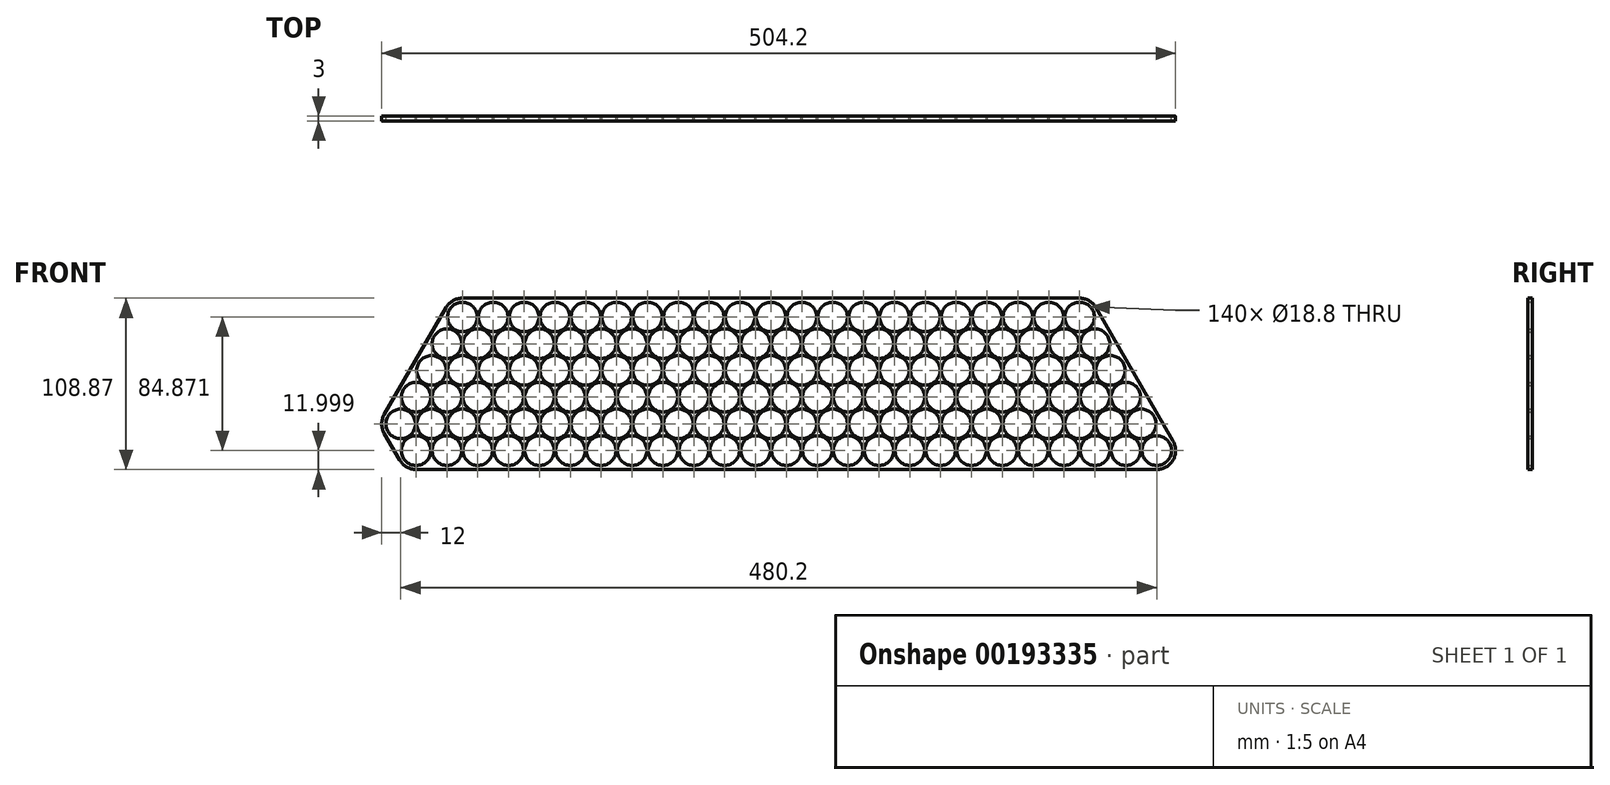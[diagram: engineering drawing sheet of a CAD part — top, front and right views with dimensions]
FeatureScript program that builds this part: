
annotation { "Feature Type Name" : "Feature", "Feature Type Description" : "" }
export const myFeature = defineFeature(function(context is Context, id is Id, definition is map)
    precondition{}
    {
        {
            var Q0;
            Q0=qCreatedBy(makeId("Front.planeOp"),FACE);
            var sketch = newSketch(context, id + "F0", { "sketchPlane" : qUnion([Q0])});
            skLineSegment(sketch, "E0", {"start": v(0, 0) * mm, "end": v(79.44, 0) * mm, "construction": true});
            skLineSegment(sketch, "E1", {"start": v(0, 0) * mm, "end": v(43.4, -75.16) * mm, "construction": true});
            skCircle(sketch, "E2", {"center": v(0, 0) * mm, "radius": 9.4 * mm});
            skCircle(sketch, "E3.1.0.0", {"center": v(19.6, 0) * mm, "radius": 9.4 * mm});
            skCircle(sketch, "E3.2.0.0", {"center": v(39.2, 0) * mm, "radius": 9.4 * mm});
            skCircle(sketch, "E3.3.0.0", {"center": v(58.8, 0) * mm, "radius": 9.4 * mm});
            skCircle(sketch, "E3.4.0.0", {"center": v(78.4, 0) * mm, "radius": 9.4 * mm});
            skCircle(sketch, "E3.5.0.0", {"center": v(98, 0) * mm, "radius": 9.4 * mm});
            skCircle(sketch, "E3.6.0.0", {"center": v(117.6, 0) * mm, "radius": 9.4 * mm});
            skCircle(sketch, "E3.7.0.0", {"center": v(137.2, 0) * mm, "radius": 9.4 * mm});
            skCircle(sketch, "E3.8.0.0", {"center": v(156.8, 0) * mm, "radius": 9.4 * mm});
            skCircle(sketch, "E3.9.0.0", {"center": v(176.4, 0) * mm, "radius": 9.4 * mm});
            skCircle(sketch, "E3.10.0.0", {"center": v(196, 0) * mm, "radius": 9.4 * mm});
            skCircle(sketch, "E3.11.0.0", {"center": v(215.6, 0) * mm, "radius": 9.4 * mm});
            skCircle(sketch, "E3.12.0.0", {"center": v(235.2, 0) * mm, "radius": 9.4 * mm});
            skCircle(sketch, "E3.13.0.0", {"center": v(254.8, 0) * mm, "radius": 9.4 * mm});
            skCircle(sketch, "E3.14.0.0", {"center": v(274.4, 0) * mm, "radius": 9.4 * mm});
            skCircle(sketch, "E3.15.0.0", {"center": v(294, 0) * mm, "radius": 9.4 * mm});
            skCircle(sketch, "E3.16.0.0", {"center": v(313.6, 0) * mm, "radius": 9.4 * mm});
            skCircle(sketch, "E3.17.0.0", {"center": v(333.2, 0) * mm, "radius": 9.4 * mm});
            skCircle(sketch, "E3.18.0.0", {"center": v(352.8, 0) * mm, "radius": 9.4 * mm});
            skCircle(sketch, "E3.19.0.0", {"center": v(372.4, 0) * mm, "radius": 9.4 * mm});
            skLineSegment(sketch, "E3.direction1", {"start": v(0, 0) * mm, "end": v(19.6, 0) * mm, "construction": true});
            skCircle(sketch, "E4.1.0.0", {"center": v(9.8, -16.97) * mm, "radius": 9.4 * mm});
            skCircle(sketch, "E4.2.0.0", {"center": v(19.6, -33.95) * mm, "radius": 9.4 * mm});
            skCircle(sketch, "E4.3.0.0", {"center": v(29.4, -50.92) * mm, "radius": 9.4 * mm});
            skCircle(sketch, "E4.4.0.0", {"center": v(39.2, -67.9) * mm, "radius": 9.4 * mm});
            skCircle(sketch, "E4.5.0.0", {"center": v(49, -84.87) * mm, "radius": 9.4 * mm});
            skLineSegment(sketch, "E4.direction1", {"start": v(0, 0) * mm, "end": v(9.8, -16.97) * mm, "construction": true});
            skCircle(sketch, "E5.1.0.0", {"center": v(29.4, -16.97) * mm, "radius": 9.4 * mm});
            skCircle(sketch, "E5.1.0.1", {"center": v(39.2, -33.95) * mm, "radius": 9.4 * mm});
            skCircle(sketch, "E5.1.0.2", {"center": v(49, -50.92) * mm, "radius": 9.4 * mm});
            skCircle(sketch, "E5.1.0.3", {"center": v(58.8, -67.9) * mm, "radius": 9.4 * mm});
            skCircle(sketch, "E5.1.0.4", {"center": v(68.6, -84.87) * mm, "radius": 9.4 * mm});
            skCircle(sketch, "E5.2.0.0", {"center": v(49, -16.97) * mm, "radius": 9.4 * mm});
            skCircle(sketch, "E5.2.0.1", {"center": v(58.8, -33.95) * mm, "radius": 9.4 * mm});
            skCircle(sketch, "E5.2.0.2", {"center": v(68.6, -50.92) * mm, "radius": 9.4 * mm});
            skCircle(sketch, "E5.2.0.3", {"center": v(78.4, -67.9) * mm, "radius": 9.4 * mm});
            skCircle(sketch, "E5.2.0.4", {"center": v(88.2, -84.87) * mm, "radius": 9.4 * mm});
            skCircle(sketch, "E5.3.0.0", {"center": v(68.6, -16.97) * mm, "radius": 9.4 * mm});
            skCircle(sketch, "E5.3.0.1", {"center": v(78.4, -33.95) * mm, "radius": 9.4 * mm});
            skCircle(sketch, "E5.3.0.2", {"center": v(88.2, -50.92) * mm, "radius": 9.4 * mm});
            skCircle(sketch, "E5.3.0.3", {"center": v(98, -67.9) * mm, "radius": 9.4 * mm});
            skCircle(sketch, "E5.3.0.4", {"center": v(107.8, -84.87) * mm, "radius": 9.4 * mm});
            skCircle(sketch, "E5.4.0.0", {"center": v(88.2, -16.97) * mm, "radius": 9.4 * mm});
            skCircle(sketch, "E5.4.0.1", {"center": v(98, -33.95) * mm, "radius": 9.4 * mm});
            skCircle(sketch, "E5.4.0.2", {"center": v(107.8, -50.92) * mm, "radius": 9.4 * mm});
            skCircle(sketch, "E5.4.0.3", {"center": v(117.6, -67.9) * mm, "radius": 9.4 * mm});
            skCircle(sketch, "E5.4.0.4", {"center": v(127.4, -84.87) * mm, "radius": 9.4 * mm});
            skCircle(sketch, "E5.5.0.0", {"center": v(107.8, -16.97) * mm, "radius": 9.4 * mm});
            skCircle(sketch, "E5.5.0.1", {"center": v(117.6, -33.95) * mm, "radius": 9.4 * mm});
            skCircle(sketch, "E5.5.0.2", {"center": v(127.4, -50.92) * mm, "radius": 9.4 * mm});
            skCircle(sketch, "E5.5.0.3", {"center": v(137.2, -67.9) * mm, "radius": 9.4 * mm});
            skCircle(sketch, "E5.5.0.4", {"center": v(147, -84.87) * mm, "radius": 9.4 * mm});
            skCircle(sketch, "E5.6.0.0", {"center": v(127.4, -16.97) * mm, "radius": 9.4 * mm});
            skCircle(sketch, "E5.6.0.1", {"center": v(137.2, -33.95) * mm, "radius": 9.4 * mm});
            skCircle(sketch, "E5.6.0.2", {"center": v(147, -50.92) * mm, "radius": 9.4 * mm});
            skCircle(sketch, "E5.6.0.3", {"center": v(156.8, -67.9) * mm, "radius": 9.4 * mm});
            skCircle(sketch, "E5.6.0.4", {"center": v(166.6, -84.87) * mm, "radius": 9.4 * mm});
            skCircle(sketch, "E5.7.0.0", {"center": v(147, -16.97) * mm, "radius": 9.4 * mm});
            skCircle(sketch, "E5.7.0.1", {"center": v(156.8, -33.95) * mm, "radius": 9.4 * mm});
            skCircle(sketch, "E5.7.0.2", {"center": v(166.6, -50.92) * mm, "radius": 9.4 * mm});
            skCircle(sketch, "E5.7.0.3", {"center": v(176.4, -67.9) * mm, "radius": 9.4 * mm});
            skCircle(sketch, "E5.7.0.4", {"center": v(186.2, -84.87) * mm, "radius": 9.4 * mm});
            skCircle(sketch, "E5.8.0.0", {"center": v(166.6, -16.97) * mm, "radius": 9.4 * mm});
            skCircle(sketch, "E5.8.0.1", {"center": v(176.4, -33.95) * mm, "radius": 9.4 * mm});
            skCircle(sketch, "E5.8.0.2", {"center": v(186.2, -50.92) * mm, "radius": 9.4 * mm});
            skCircle(sketch, "E5.8.0.3", {"center": v(196, -67.9) * mm, "radius": 9.4 * mm});
            skCircle(sketch, "E5.8.0.4", {"center": v(205.8, -84.87) * mm, "radius": 9.4 * mm});
            skCircle(sketch, "E5.9.0.0", {"center": v(186.2, -16.97) * mm, "radius": 9.4 * mm});
            skCircle(sketch, "E5.9.0.1", {"center": v(196, -33.95) * mm, "radius": 9.4 * mm});
            skCircle(sketch, "E5.9.0.2", {"center": v(205.8, -50.92) * mm, "radius": 9.4 * mm});
            skCircle(sketch, "E5.9.0.3", {"center": v(215.6, -67.9) * mm, "radius": 9.4 * mm});
            skCircle(sketch, "E5.9.0.4", {"center": v(225.4, -84.87) * mm, "radius": 9.4 * mm});
            skCircle(sketch, "E5.10.0.0", {"center": v(205.8, -16.97) * mm, "radius": 9.4 * mm});
            skCircle(sketch, "E5.10.0.1", {"center": v(215.6, -33.95) * mm, "radius": 9.4 * mm});
            skCircle(sketch, "E5.10.0.2", {"center": v(225.4, -50.92) * mm, "radius": 9.4 * mm});
            skCircle(sketch, "E5.10.0.3", {"center": v(235.2, -67.9) * mm, "radius": 9.4 * mm});
            skCircle(sketch, "E5.10.0.4", {"center": v(245, -84.87) * mm, "radius": 9.4 * mm});
            skCircle(sketch, "E5.11.0.0", {"center": v(225.4, -16.97) * mm, "radius": 9.4 * mm});
            skCircle(sketch, "E5.11.0.1", {"center": v(235.2, -33.95) * mm, "radius": 9.4 * mm});
            skCircle(sketch, "E5.11.0.2", {"center": v(245, -50.92) * mm, "radius": 9.4 * mm});
            skCircle(sketch, "E5.11.0.3", {"center": v(254.8, -67.9) * mm, "radius": 9.4 * mm});
            skCircle(sketch, "E5.11.0.4", {"center": v(264.6, -84.87) * mm, "radius": 9.4 * mm});
            skCircle(sketch, "E5.12.0.0", {"center": v(245, -16.97) * mm, "radius": 9.4 * mm});
            skCircle(sketch, "E5.12.0.1", {"center": v(254.8, -33.95) * mm, "radius": 9.4 * mm});
            skCircle(sketch, "E5.12.0.2", {"center": v(264.6, -50.92) * mm, "radius": 9.4 * mm});
            skCircle(sketch, "E5.12.0.3", {"center": v(274.4, -67.9) * mm, "radius": 9.4 * mm});
            skCircle(sketch, "E5.12.0.4", {"center": v(284.2, -84.87) * mm, "radius": 9.4 * mm});
            skCircle(sketch, "E5.13.0.0", {"center": v(264.6, -16.97) * mm, "radius": 9.4 * mm});
            skCircle(sketch, "E5.13.0.1", {"center": v(274.4, -33.95) * mm, "radius": 9.4 * mm});
            skCircle(sketch, "E5.13.0.2", {"center": v(284.2, -50.92) * mm, "radius": 9.4 * mm});
            skCircle(sketch, "E5.13.0.3", {"center": v(294, -67.9) * mm, "radius": 9.4 * mm});
            skCircle(sketch, "E5.13.0.4", {"center": v(303.8, -84.87) * mm, "radius": 9.4 * mm});
            skCircle(sketch, "E5.14.0.0", {"center": v(284.2, -16.97) * mm, "radius": 9.4 * mm});
            skCircle(sketch, "E5.14.0.1", {"center": v(294, -33.95) * mm, "radius": 9.4 * mm});
            skCircle(sketch, "E5.14.0.2", {"center": v(303.8, -50.92) * mm, "radius": 9.4 * mm});
            skCircle(sketch, "E5.14.0.3", {"center": v(313.6, -67.9) * mm, "radius": 9.4 * mm});
            skCircle(sketch, "E5.14.0.4", {"center": v(323.4, -84.87) * mm, "radius": 9.4 * mm});
            skCircle(sketch, "E5.15.0.0", {"center": v(303.8, -16.97) * mm, "radius": 9.4 * mm});
            skCircle(sketch, "E5.15.0.1", {"center": v(313.6, -33.95) * mm, "radius": 9.4 * mm});
            skCircle(sketch, "E5.15.0.2", {"center": v(323.4, -50.92) * mm, "radius": 9.4 * mm});
            skCircle(sketch, "E5.15.0.3", {"center": v(333.2, -67.9) * mm, "radius": 9.4 * mm});
            skCircle(sketch, "E5.15.0.4", {"center": v(343, -84.87) * mm, "radius": 9.4 * mm});
            skCircle(sketch, "E5.16.0.0", {"center": v(323.4, -16.97) * mm, "radius": 9.4 * mm});
            skCircle(sketch, "E5.16.0.1", {"center": v(333.2, -33.95) * mm, "radius": 9.4 * mm});
            skCircle(sketch, "E5.16.0.2", {"center": v(343, -50.92) * mm, "radius": 9.4 * mm});
            skCircle(sketch, "E5.16.0.3", {"center": v(352.8, -67.9) * mm, "radius": 9.4 * mm});
            skCircle(sketch, "E5.16.0.4", {"center": v(362.6, -84.87) * mm, "radius": 9.4 * mm});
            skCircle(sketch, "E5.17.0.0", {"center": v(343, -16.97) * mm, "radius": 9.4 * mm});
            skCircle(sketch, "E5.17.0.1", {"center": v(352.8, -33.95) * mm, "radius": 9.4 * mm});
            skCircle(sketch, "E5.17.0.2", {"center": v(362.6, -50.92) * mm, "radius": 9.4 * mm});
            skCircle(sketch, "E5.17.0.3", {"center": v(372.4, -67.9) * mm, "radius": 9.4 * mm});
            skCircle(sketch, "E5.17.0.4", {"center": v(382.2, -84.87) * mm, "radius": 9.4 * mm});
            skCircle(sketch, "E5.18.0.0", {"center": v(362.6, -16.97) * mm, "radius": 9.4 * mm});
            skCircle(sketch, "E5.18.0.1", {"center": v(372.4, -33.95) * mm, "radius": 9.4 * mm});
            skCircle(sketch, "E5.18.0.2", {"center": v(382.2, -50.92) * mm, "radius": 9.4 * mm});
            skCircle(sketch, "E5.18.0.3", {"center": v(392, -67.9) * mm, "radius": 9.4 * mm});
            skCircle(sketch, "E5.18.0.4", {"center": v(401.8, -84.87) * mm, "radius": 9.4 * mm});
            skCircle(sketch, "E5.19.0.0", {"center": v(382.2, -16.97) * mm, "radius": 9.4 * mm});
            skCircle(sketch, "E5.19.0.1", {"center": v(392, -33.95) * mm, "radius": 9.4 * mm});
            skCircle(sketch, "E5.19.0.2", {"center": v(401.8, -50.92) * mm, "radius": 9.4 * mm});
            skCircle(sketch, "E5.19.0.3", {"center": v(411.6, -67.9) * mm, "radius": 9.4 * mm});
            skCircle(sketch, "E5.19.0.4", {"center": v(421.4, -84.87) * mm, "radius": 9.4 * mm});
            skLineSegment(sketch, "E5.direction1", {"start": v(9.8, -16.97) * mm, "end": v(29.4, -16.97) * mm, "construction": true});
            skLineSegment(sketch, "E6", {"start": v(0, 0) * mm, "end": v(372.4, 0) * mm, "construction": true});
            skLineSegment(sketch, "E7", {"start": v(372.4, 0) * mm, "end": v(421.4, -84.87) * mm, "construction": true});
            skLineSegment(sketch, "E8", {"start": v(49, -84.87) * mm, "end": v(0, 0) * mm, "construction": true});
            skLineSegment(sketch, "E9.0", {"start": v(-20.78, 12) * mm, "end": v(372.4, 12) * mm});
            skLineSegment(sketch, "E9.1", {"start": v(42.07, -96.87) * mm, "end": v(-20.78, 12) * mm, "construction": true});
            skLineSegment(sketch, "E10", {"start": v(49, -84.87) * mm, "end": v(421.4, -84.87) * mm, "construction": true});
            skLineSegment(sketch, "E11.0", {"start": v(49, -96.87) * mm, "end": v(421.4, -96.87) * mm});
            skLineSegment(sketch, "E12", {"start": v(49, -96.87) * mm, "end": v(42.07, -96.87) * mm});
            skLineSegment(sketch, "E13", {"start": v(42.07, -96.87) * mm, "end": v(-49, -96.87) * mm});
            skPoint(sketch, "E13.endSnap0", {"position": v(45.54, -96.87) * mm});
            skLineSegment(sketch, "E14", {"start": v(-20.78, 12) * mm, "end": v(-20.84, 11.94) * mm});
            skCircle(sketch, "E15.1.0.0", {"center": v(29.4, -84.87) * mm, "radius": 9.4 * mm});
            skCircle(sketch, "E15.2.0.0", {"center": v(9.8, -84.87) * mm, "radius": 9.4 * mm});
            skCircle(sketch, "E15.3.0.0", {"center": v(-9.8, -84.87) * mm, "radius": 9.4 * mm});
            skCircle(sketch, "E15.4.0.0", {"center": v(-29.4, -84.87) * mm, "radius": 9.4 * mm});
            skCircle(sketch, "E15.5.0.0", {"center": v(-49, -84.87) * mm, "radius": 9.4 * mm});
            skLineSegment(sketch, "E15.direction1", {"start": v(49, -84.87) * mm, "end": v(29.4, -84.87) * mm, "construction": true});
            skCircle(sketch, "E16.1.0.0", {"center": v(19.6, -67.9) * mm, "radius": 9.4 * mm});
            skCircle(sketch, "E16.2.0.0", {"center": v(0, -67.9) * mm, "radius": 9.4 * mm});
            skCircle(sketch, "E16.3.0.0", {"center": v(-19.6, -67.9) * mm, "radius": 9.4 * mm});
            skCircle(sketch, "E16.4.0.0", {"center": v(-39.2, -67.9) * mm, "radius": 9.4 * mm});
            skCircle(sketch, "E16.5.0.0", {"center": v(-58.8, -67.9) * mm, "radius": 9.4 * mm});
            skLineSegment(sketch, "E16.direction1", {"start": v(39.2, -67.9) * mm, "end": v(19.6, -67.9) * mm, "construction": true});
            skCircle(sketch, "E17.1.0.0", {"center": v(9.8, -50.92) * mm, "radius": 9.4 * mm});
            skCircle(sketch, "E17.2.0.0", {"center": v(-9.8, -50.92) * mm, "radius": 9.4 * mm});
            skCircle(sketch, "E17.3.0.0", {"center": v(-29.4, -50.92) * mm, "radius": 9.4 * mm});
            skCircle(sketch, "E17.4.0.0", {"center": v(-49, -50.92) * mm, "radius": 9.4 * mm});
            skLineSegment(sketch, "E17.direction1", {"start": v(29.4, -50.92) * mm, "end": v(9.8, -50.92) * mm, "construction": true});
            skCircle(sketch, "E18.1.0.0", {"center": v(0, -33.95) * mm, "radius": 9.4 * mm});
            skCircle(sketch, "E18.2.0.0", {"center": v(-19.6, -33.95) * mm, "radius": 9.4 * mm});
            skCircle(sketch, "E18.3.0.0", {"center": v(-39.2, -33.95) * mm, "radius": 9.4 * mm});
            skLineSegment(sketch, "E18.direction1", {"start": v(19.6, -33.95) * mm, "end": v(0, -33.95) * mm, "construction": true});
            skCircle(sketch, "E19.1.0.0", {"center": v(-9.8, -16.97) * mm, "radius": 9.4 * mm});
            skCircle(sketch, "E19.2.0.0", {"center": v(-29.4, -16.97) * mm, "radius": 9.4 * mm});
            skLineSegment(sketch, "E19.direction1", {"start": v(9.8, -16.97) * mm, "end": v(-9.8, -16.97) * mm, "construction": true});
            skCircle(sketch, "E20.1.0.0", {"center": v(-19.6, 0) * mm, "radius": 9.4 * mm});
            skLineSegment(sketch, "E20.direction1", {"start": v(0, 0) * mm, "end": v(-19.6, 0) * mm, "construction": true});
            skArc(sketch, "E21.0", {"start": v(-19.6, 12) * mm, "mid": v(-25.6, 10.4) * mm, "end": v(-30, 6) * mm});
            skLineSegment(sketch, "E22", {"start": v(-30, 6) * mm, "end": v(-69.2, -61.9) * mm});
            skPoint(sketch, "E23.orphan", {"position": v(-115.18, -96.87) * mm});
            skArc(sketch, "E24.trimOffspring", {"start": v(-69.2, -61.9) * mm, "mid": v(-70.8, -67.9) * mm, "end": v(-69.2, -73.9) * mm});
            skLineSegment(sketch, "E25", {"start": v(-59.4, -90.87) * mm, "end": v(-69.2, -73.9) * mm});
            skArc(sketch, "E26.trimOffspring", {"start": v(-59.4, -90.87) * mm, "mid": v(-55, -95.26) * mm, "end": v(-49, -96.87) * mm});
            skArc(sketch, "E27", {"start": v(421.4, -96.87) * mm, "mid": v(431.8, -90.87) * mm, "end": v(431.8, -78.87) * mm});
            skArc(sketch, "E28", {"start": v(382.8, 6) * mm, "mid": v(378.4, 10.4) * mm, "end": v(372.4, 12) * mm});
            skLineSegment(sketch, "E29", {"start": v(431.8, -78.87) * mm, "end": v(382.8, 6) * mm});
            skSolve(sketch);
        }
        {
            var Q0;
            Q0=makeQuery(id+"F0.imprint","IMPRINT",FACE,{"disambiguationData":[TD([[makeQuery(id+"F0.imprint","IMPRINT",EDGE,{"derivedFrom":sQuery(id+"F0.wireOp",EDGE,"E2")}),-1.0]])]});
            extrude(context, id + "F1", {"entities" : qUnion([Q0]), "depth" : 3 * mm});
        }
        {
            var Q0;
            Q0=makeQuery(id+"F0.imprint","IMPRINT",FACE,{"disambiguationData":[TD([[makeQuery(id+"F0.imprint","IMPRINT",EDGE,{"derivedFrom":sQuery(id+"F0.wireOp",EDGE,"E2")}),-1.0]])]});
            var Q1;
            Q1=makeQuery(id+"F0.imprint","IMPRINT",FACE,{"disambiguationData":[TD([[makeQuery(id+"F0.imprint","IMPRINT",EDGE,{"derivedFrom":sQuery(id+"F0.wireOp",EDGE,"E3.19.0.0")}),1.0]])]});
            var Q2;
            Q2=makeQuery(id+"F0.imprint","IMPRINT",FACE,{"disambiguationData":[TD([[makeQuery(id+"F0.imprint","IMPRINT",EDGE,{"derivedFrom":sQuery(id+"F0.wireOp",EDGE,"E3.18.0.0")}),1.0]])]});
            var Q3;
            Q3=makeQuery(id+"F0.imprint","IMPRINT",FACE,{"disambiguationData":[TD([[makeQuery(id+"F0.imprint","IMPRINT",EDGE,{"derivedFrom":sQuery(id+"F0.wireOp",EDGE,"E3.17.0.0")}),1.0]])]});
            var Q4;
            Q4=makeQuery(id+"F0.imprint","IMPRINT",FACE,{"disambiguationData":[TD([[makeQuery(id+"F0.imprint","IMPRINT",EDGE,{"derivedFrom":sQuery(id+"F0.wireOp",EDGE,"E3.16.0.0")}),1.0]])]});
            var Q5;
            Q5=makeQuery(id+"F0.imprint","IMPRINT",FACE,{"disambiguationData":[TD([[makeQuery(id+"F0.imprint","IMPRINT",EDGE,{"derivedFrom":sQuery(id+"F0.wireOp",EDGE,"E3.15.0.0")}),1.0]])]});
            var Q6;
            Q6=makeQuery(id+"F0.imprint","IMPRINT",FACE,{"disambiguationData":[TD([[makeQuery(id+"F0.imprint","IMPRINT",EDGE,{"derivedFrom":sQuery(id+"F0.wireOp",EDGE,"E3.14.0.0")}),1.0]])]});
            var Q7;
            Q7=makeQuery(id+"F0.imprint","IMPRINT",FACE,{"disambiguationData":[TD([[makeQuery(id+"F0.imprint","IMPRINT",EDGE,{"derivedFrom":sQuery(id+"F0.wireOp",EDGE,"E3.13.0.0")}),1.0]])]});
            var Q8;
            Q8=makeQuery(id+"F0.imprint","IMPRINT",FACE,{"disambiguationData":[TD([[makeQuery(id+"F0.imprint","IMPRINT",EDGE,{"derivedFrom":sQuery(id+"F0.wireOp",EDGE,"E3.12.0.0")}),1.0]])]});
            var Q9;
            Q9=makeQuery(id+"F0.imprint","IMPRINT",FACE,{"disambiguationData":[TD([[makeQuery(id+"F0.imprint","IMPRINT",EDGE,{"derivedFrom":sQuery(id+"F0.wireOp",EDGE,"E3.11.0.0")}),1.0]])]});
            var Q10;
            Q10=makeQuery(id+"F0.imprint","IMPRINT",FACE,{"disambiguationData":[TD([[makeQuery(id+"F0.imprint","IMPRINT",EDGE,{"derivedFrom":sQuery(id+"F0.wireOp",EDGE,"E3.10.0.0")}),1.0]])]});
            var Q11;
            Q11=makeQuery(id+"F0.imprint","IMPRINT",FACE,{"disambiguationData":[TD([[makeQuery(id+"F0.imprint","IMPRINT",EDGE,{"derivedFrom":sQuery(id+"F0.wireOp",EDGE,"E3.9.0.0")}),1.0]])]});
            var Q12;
            Q12=makeQuery(id+"F0.imprint","IMPRINT",FACE,{"disambiguationData":[TD([[makeQuery(id+"F0.imprint","IMPRINT",EDGE,{"derivedFrom":sQuery(id+"F0.wireOp",EDGE,"E3.8.0.0")}),1.0]])]});
            var Q13;
            Q13=makeQuery(id+"F0.imprint","IMPRINT",FACE,{"disambiguationData":[TD([[makeQuery(id+"F0.imprint","IMPRINT",EDGE,{"derivedFrom":sQuery(id+"F0.wireOp",EDGE,"E3.7.0.0")}),1.0]])]});
            var Q14;
            Q14=makeQuery(id+"F0.imprint","IMPRINT",FACE,{"disambiguationData":[TD([[makeQuery(id+"F0.imprint","IMPRINT",EDGE,{"derivedFrom":sQuery(id+"F0.wireOp",EDGE,"E3.6.0.0")}),1.0]])]});
            var Q15;
            Q15=makeQuery(id+"F0.imprint","IMPRINT",FACE,{"disambiguationData":[TD([[makeQuery(id+"F0.imprint","IMPRINT",EDGE,{"derivedFrom":sQuery(id+"F0.wireOp",EDGE,"E3.5.0.0")}),1.0]])]});
            var Q16;
            Q16=makeQuery(id+"F0.imprint","IMPRINT",FACE,{"disambiguationData":[TD([[makeQuery(id+"F0.imprint","IMPRINT",EDGE,{"derivedFrom":sQuery(id+"F0.wireOp",EDGE,"E3.4.0.0")}),1.0]])]});
            var Q17;
            Q17=makeQuery(id+"F0.imprint","IMPRINT",FACE,{"disambiguationData":[TD([[makeQuery(id+"F0.imprint","IMPRINT",EDGE,{"derivedFrom":sQuery(id+"F0.wireOp",EDGE,"E3.3.0.0")}),1.0]])]});
            var Q18;
            Q18=makeQuery(id+"F0.imprint","IMPRINT",FACE,{"disambiguationData":[TD([[makeQuery(id+"F0.imprint","IMPRINT",EDGE,{"derivedFrom":sQuery(id+"F0.wireOp",EDGE,"E3.2.0.0")}),1.0]])]});
            var Q19;
            Q19=makeQuery(id+"F0.imprint","IMPRINT",FACE,{"disambiguationData":[TD([[makeQuery(id+"F0.imprint","IMPRINT",EDGE,{"derivedFrom":sQuery(id+"F0.wireOp",EDGE,"E3.1.0.0")}),1.0]])]});
            var Q20;
            Q20=makeQuery(id+"F0.imprint","IMPRINT",FACE,{"disambiguationData":[TD([[makeQuery(id+"F0.imprint","IMPRINT",EDGE,{"derivedFrom":sQuery(id+"F0.wireOp",EDGE,"E2")}),1.0]])]});
            var Q21;
            Q21=makeQuery(id+"F0.imprint","IMPRINT",FACE,{"disambiguationData":[TD([[makeQuery(id+"F0.imprint","IMPRINT",EDGE,{"derivedFrom":sQuery(id+"F0.wireOp",EDGE,"E20.1.0.0")}),1.0]])]});
            var Q22;
            Q22=makeQuery(id+"F0.imprint","IMPRINT",FACE,{"disambiguationData":[TD([[makeQuery(id+"F0.imprint","IMPRINT",EDGE,{"derivedFrom":sQuery(id+"F0.wireOp",EDGE,"E19.2.0.0")}),1.0]])]});
            var Q23;
            Q23=makeQuery(id+"F0.imprint","IMPRINT",FACE,{"disambiguationData":[TD([[makeQuery(id+"F0.imprint","IMPRINT",EDGE,{"derivedFrom":sQuery(id+"F0.wireOp",EDGE,"E19.1.0.0")}),1.0]])]});
            var Q24;
            Q24=makeQuery(id+"F0.imprint","IMPRINT",FACE,{"disambiguationData":[TD([[makeQuery(id+"F0.imprint","IMPRINT",EDGE,{"derivedFrom":sQuery(id+"F0.wireOp",EDGE,"E4.1.0.0")}),1.0]])]});
            var Q25;
            Q25=makeQuery(id+"F0.imprint","IMPRINT",FACE,{"disambiguationData":[TD([[makeQuery(id+"F0.imprint","IMPRINT",EDGE,{"derivedFrom":sQuery(id+"F0.wireOp",EDGE,"E5.1.0.0")}),1.0]])]});
            var Q26;
            Q26=makeQuery(id+"F0.imprint","IMPRINT",FACE,{"disambiguationData":[TD([[makeQuery(id+"F0.imprint","IMPRINT",EDGE,{"derivedFrom":sQuery(id+"F0.wireOp",EDGE,"E5.2.0.0")}),1.0]])]});
            var Q27;
            Q27=makeQuery(id+"F0.imprint","IMPRINT",FACE,{"disambiguationData":[TD([[makeQuery(id+"F0.imprint","IMPRINT",EDGE,{"derivedFrom":sQuery(id+"F0.wireOp",EDGE,"E5.3.0.0")}),1.0]])]});
            var Q28;
            Q28=makeQuery(id+"F0.imprint","IMPRINT",FACE,{"disambiguationData":[TD([[makeQuery(id+"F0.imprint","IMPRINT",EDGE,{"derivedFrom":sQuery(id+"F0.wireOp",EDGE,"E5.4.0.0")}),1.0]])]});
            var Q29;
            Q29=makeQuery(id+"F0.imprint","IMPRINT",FACE,{"disambiguationData":[TD([[makeQuery(id+"F0.imprint","IMPRINT",EDGE,{"derivedFrom":sQuery(id+"F0.wireOp",EDGE,"E5.5.0.0")}),1.0]])]});
            var Q30;
            Q30=makeQuery(id+"F0.imprint","IMPRINT",FACE,{"disambiguationData":[TD([[makeQuery(id+"F0.imprint","IMPRINT",EDGE,{"derivedFrom":sQuery(id+"F0.wireOp",EDGE,"E5.6.0.0")}),1.0]])]});
            var Q31;
            Q31=makeQuery(id+"F0.imprint","IMPRINT",FACE,{"disambiguationData":[TD([[makeQuery(id+"F0.imprint","IMPRINT",EDGE,{"derivedFrom":sQuery(id+"F0.wireOp",EDGE,"E5.7.0.0")}),1.0]])]});
            var Q32;
            Q32=makeQuery(id+"F0.imprint","IMPRINT",FACE,{"disambiguationData":[TD([[makeQuery(id+"F0.imprint","IMPRINT",EDGE,{"derivedFrom":sQuery(id+"F0.wireOp",EDGE,"E5.8.0.0")}),1.0]])]});
            var Q33;
            Q33=makeQuery(id+"F0.imprint","IMPRINT",FACE,{"disambiguationData":[TD([[makeQuery(id+"F0.imprint","IMPRINT",EDGE,{"derivedFrom":sQuery(id+"F0.wireOp",EDGE,"E5.9.0.0")}),1.0]])]});
            var Q34;
            Q34=makeQuery(id+"F0.imprint","IMPRINT",FACE,{"disambiguationData":[TD([[makeQuery(id+"F0.imprint","IMPRINT",EDGE,{"derivedFrom":sQuery(id+"F0.wireOp",EDGE,"E5.10.0.0")}),1.0]])]});
            var Q35;
            Q35=makeQuery(id+"F0.imprint","IMPRINT",FACE,{"disambiguationData":[TD([[makeQuery(id+"F0.imprint","IMPRINT",EDGE,{"derivedFrom":sQuery(id+"F0.wireOp",EDGE,"E5.11.0.0")}),1.0]])]});
            var Q36;
            Q36=makeQuery(id+"F0.imprint","IMPRINT",FACE,{"disambiguationData":[TD([[makeQuery(id+"F0.imprint","IMPRINT",EDGE,{"derivedFrom":sQuery(id+"F0.wireOp",EDGE,"E5.12.0.0")}),1.0]])]});
            var Q37;
            Q37=makeQuery(id+"F0.imprint","IMPRINT",FACE,{"disambiguationData":[TD([[makeQuery(id+"F0.imprint","IMPRINT",EDGE,{"derivedFrom":sQuery(id+"F0.wireOp",EDGE,"E5.13.0.0")}),1.0]])]});
            var Q38;
            Q38=makeQuery(id+"F0.imprint","IMPRINT",FACE,{"disambiguationData":[TD([[makeQuery(id+"F0.imprint","IMPRINT",EDGE,{"derivedFrom":sQuery(id+"F0.wireOp",EDGE,"E5.14.0.0")}),1.0]])]});
            var Q39;
            Q39=makeQuery(id+"F0.imprint","IMPRINT",FACE,{"disambiguationData":[TD([[makeQuery(id+"F0.imprint","IMPRINT",EDGE,{"derivedFrom":sQuery(id+"F0.wireOp",EDGE,"E5.15.0.0")}),1.0]])]});
            var Q40;
            Q40=makeQuery(id+"F0.imprint","IMPRINT",FACE,{"disambiguationData":[TD([[makeQuery(id+"F0.imprint","IMPRINT",EDGE,{"derivedFrom":sQuery(id+"F0.wireOp",EDGE,"E5.16.0.0")}),1.0]])]});
            var Q41;
            Q41=makeQuery(id+"F0.imprint","IMPRINT",FACE,{"disambiguationData":[TD([[makeQuery(id+"F0.imprint","IMPRINT",EDGE,{"derivedFrom":sQuery(id+"F0.wireOp",EDGE,"E5.17.0.0")}),1.0]])]});
            var Q42;
            Q42=makeQuery(id+"F0.imprint","IMPRINT",FACE,{"disambiguationData":[TD([[makeQuery(id+"F0.imprint","IMPRINT",EDGE,{"derivedFrom":sQuery(id+"F0.wireOp",EDGE,"E5.18.0.0")}),1.0]])]});
            var Q43;
            Q43=makeQuery(id+"F0.imprint","IMPRINT",FACE,{"disambiguationData":[TD([[makeQuery(id+"F0.imprint","IMPRINT",EDGE,{"derivedFrom":sQuery(id+"F0.wireOp",EDGE,"E5.19.0.0")}),1.0]])]});
            var Q44;
            Q44=makeQuery(id+"F0.imprint","IMPRINT",FACE,{"disambiguationData":[TD([[makeQuery(id+"F0.imprint","IMPRINT",EDGE,{"derivedFrom":sQuery(id+"F0.wireOp",EDGE,"E5.19.0.1")}),1.0]])]});
            var Q45;
            Q45=makeQuery(id+"F0.imprint","IMPRINT",FACE,{"disambiguationData":[TD([[makeQuery(id+"F0.imprint","IMPRINT",EDGE,{"derivedFrom":sQuery(id+"F0.wireOp",EDGE,"E5.18.0.1")}),1.0]])]});
            var Q46;
            Q46=makeQuery(id+"F0.imprint","IMPRINT",FACE,{"disambiguationData":[TD([[makeQuery(id+"F0.imprint","IMPRINT",EDGE,{"derivedFrom":sQuery(id+"F0.wireOp",EDGE,"E5.17.0.1")}),1.0]])]});
            var Q47;
            Q47=makeQuery(id+"F0.imprint","IMPRINT",FACE,{"disambiguationData":[TD([[makeQuery(id+"F0.imprint","IMPRINT",EDGE,{"derivedFrom":sQuery(id+"F0.wireOp",EDGE,"E5.16.0.1")}),1.0]])]});
            var Q48;
            Q48=makeQuery(id+"F0.imprint","IMPRINT",FACE,{"disambiguationData":[TD([[makeQuery(id+"F0.imprint","IMPRINT",EDGE,{"derivedFrom":sQuery(id+"F0.wireOp",EDGE,"E5.15.0.1")}),1.0]])]});
            var Q49;
            Q49=makeQuery(id+"F0.imprint","IMPRINT",FACE,{"disambiguationData":[TD([[makeQuery(id+"F0.imprint","IMPRINT",EDGE,{"derivedFrom":sQuery(id+"F0.wireOp",EDGE,"E5.14.0.1")}),1.0]])]});
            var Q50;
            Q50=makeQuery(id+"F0.imprint","IMPRINT",FACE,{"disambiguationData":[TD([[makeQuery(id+"F0.imprint","IMPRINT",EDGE,{"derivedFrom":sQuery(id+"F0.wireOp",EDGE,"E5.13.0.1")}),1.0]])]});
            var Q51;
            Q51=makeQuery(id+"F0.imprint","IMPRINT",FACE,{"disambiguationData":[TD([[makeQuery(id+"F0.imprint","IMPRINT",EDGE,{"derivedFrom":sQuery(id+"F0.wireOp",EDGE,"E5.12.0.1")}),1.0]])]});
            var Q52;
            Q52=makeQuery(id+"F0.imprint","IMPRINT",FACE,{"disambiguationData":[TD([[makeQuery(id+"F0.imprint","IMPRINT",EDGE,{"derivedFrom":sQuery(id+"F0.wireOp",EDGE,"E5.11.0.1")}),1.0]])]});
            var Q53;
            Q53=makeQuery(id+"F0.imprint","IMPRINT",FACE,{"disambiguationData":[TD([[makeQuery(id+"F0.imprint","IMPRINT",EDGE,{"derivedFrom":sQuery(id+"F0.wireOp",EDGE,"E5.10.0.1")}),1.0]])]});
            var Q54;
            Q54=makeQuery(id+"F0.imprint","IMPRINT",FACE,{"disambiguationData":[TD([[makeQuery(id+"F0.imprint","IMPRINT",EDGE,{"derivedFrom":sQuery(id+"F0.wireOp",EDGE,"E5.9.0.1")}),1.0]])]});
            var Q55;
            Q55=makeQuery(id+"F0.imprint","IMPRINT",FACE,{"disambiguationData":[TD([[makeQuery(id+"F0.imprint","IMPRINT",EDGE,{"derivedFrom":sQuery(id+"F0.wireOp",EDGE,"E5.8.0.1")}),1.0]])]});
            var Q56;
            Q56=makeQuery(id+"F0.imprint","IMPRINT",FACE,{"disambiguationData":[TD([[makeQuery(id+"F0.imprint","IMPRINT",EDGE,{"derivedFrom":sQuery(id+"F0.wireOp",EDGE,"E5.7.0.1")}),1.0]])]});
            var Q57;
            Q57=makeQuery(id+"F0.imprint","IMPRINT",FACE,{"disambiguationData":[TD([[makeQuery(id+"F0.imprint","IMPRINT",EDGE,{"derivedFrom":sQuery(id+"F0.wireOp",EDGE,"E5.6.0.1")}),1.0]])]});
            var Q58;
            Q58=makeQuery(id+"F0.imprint","IMPRINT",FACE,{"disambiguationData":[TD([[makeQuery(id+"F0.imprint","IMPRINT",EDGE,{"derivedFrom":sQuery(id+"F0.wireOp",EDGE,"E5.5.0.1")}),1.0]])]});
            var Q59;
            Q59=makeQuery(id+"F0.imprint","IMPRINT",FACE,{"disambiguationData":[TD([[makeQuery(id+"F0.imprint","IMPRINT",EDGE,{"derivedFrom":sQuery(id+"F0.wireOp",EDGE,"E5.4.0.1")}),1.0]])]});
            var Q60;
            Q60=makeQuery(id+"F0.imprint","IMPRINT",FACE,{"disambiguationData":[TD([[makeQuery(id+"F0.imprint","IMPRINT",EDGE,{"derivedFrom":sQuery(id+"F0.wireOp",EDGE,"E5.3.0.1")}),1.0]])]});
            var Q61;
            Q61=makeQuery(id+"F0.imprint","IMPRINT",FACE,{"disambiguationData":[TD([[makeQuery(id+"F0.imprint","IMPRINT",EDGE,{"derivedFrom":sQuery(id+"F0.wireOp",EDGE,"E5.2.0.1")}),1.0]])]});
            var Q62;
            Q62=makeQuery(id+"F0.imprint","IMPRINT",FACE,{"disambiguationData":[TD([[makeQuery(id+"F0.imprint","IMPRINT",EDGE,{"derivedFrom":sQuery(id+"F0.wireOp",EDGE,"E5.1.0.1")}),1.0]])]});
            var Q63;
            Q63=makeQuery(id+"F0.imprint","IMPRINT",FACE,{"disambiguationData":[TD([[makeQuery(id+"F0.imprint","IMPRINT",EDGE,{"derivedFrom":sQuery(id+"F0.wireOp",EDGE,"E4.2.0.0")}),1.0]])]});
            var Q64;
            Q64=makeQuery(id+"F0.imprint","IMPRINT",FACE,{"disambiguationData":[TD([[makeQuery(id+"F0.imprint","IMPRINT",EDGE,{"derivedFrom":sQuery(id+"F0.wireOp",EDGE,"E18.1.0.0")}),1.0]])]});
            var Q65;
            Q65=makeQuery(id+"F0.imprint","IMPRINT",FACE,{"disambiguationData":[TD([[makeQuery(id+"F0.imprint","IMPRINT",EDGE,{"derivedFrom":sQuery(id+"F0.wireOp",EDGE,"E18.2.0.0")}),1.0]])]});
            var Q66;
            Q66=makeQuery(id+"F0.imprint","IMPRINT",FACE,{"disambiguationData":[TD([[makeQuery(id+"F0.imprint","IMPRINT",EDGE,{"derivedFrom":sQuery(id+"F0.wireOp",EDGE,"E18.3.0.0")}),1.0]])]});
            var Q67;
            Q67=makeQuery(id+"F0.imprint","IMPRINT",FACE,{"disambiguationData":[TD([[makeQuery(id+"F0.imprint","IMPRINT",EDGE,{"derivedFrom":sQuery(id+"F0.wireOp",EDGE,"E17.4.0.0")}),1.0]])]});
            var Q68;
            Q68=makeQuery(id+"F0.imprint","IMPRINT",FACE,{"disambiguationData":[TD([[makeQuery(id+"F0.imprint","IMPRINT",EDGE,{"derivedFrom":sQuery(id+"F0.wireOp",EDGE,"E17.3.0.0")}),1.0]])]});
            var Q69;
            Q69=makeQuery(id+"F0.imprint","IMPRINT",FACE,{"disambiguationData":[TD([[makeQuery(id+"F0.imprint","IMPRINT",EDGE,{"derivedFrom":sQuery(id+"F0.wireOp",EDGE,"E17.2.0.0")}),1.0]])]});
            var Q70;
            Q70=makeQuery(id+"F0.imprint","IMPRINT",FACE,{"disambiguationData":[TD([[makeQuery(id+"F0.imprint","IMPRINT",EDGE,{"derivedFrom":sQuery(id+"F0.wireOp",EDGE,"E17.1.0.0")}),1.0]])]});
            var Q71;
            Q71=makeQuery(id+"F0.imprint","IMPRINT",FACE,{"disambiguationData":[TD([[makeQuery(id+"F0.imprint","IMPRINT",EDGE,{"derivedFrom":sQuery(id+"F0.wireOp",EDGE,"E4.3.0.0")}),1.0]])]});
            var Q72;
            Q72=makeQuery(id+"F0.imprint","IMPRINT",FACE,{"disambiguationData":[TD([[makeQuery(id+"F0.imprint","IMPRINT",EDGE,{"derivedFrom":sQuery(id+"F0.wireOp",EDGE,"E5.1.0.2")}),1.0]])]});
            var Q73;
            Q73=makeQuery(id+"F0.imprint","IMPRINT",FACE,{"disambiguationData":[TD([[makeQuery(id+"F0.imprint","IMPRINT",EDGE,{"derivedFrom":sQuery(id+"F0.wireOp",EDGE,"E5.2.0.2")}),1.0]])]});
            var Q74;
            Q74=makeQuery(id+"F0.imprint","IMPRINT",FACE,{"disambiguationData":[TD([[makeQuery(id+"F0.imprint","IMPRINT",EDGE,{"derivedFrom":sQuery(id+"F0.wireOp",EDGE,"E5.3.0.2")}),1.0]])]});
            var Q75;
            Q75=makeQuery(id+"F0.imprint","IMPRINT",FACE,{"disambiguationData":[TD([[makeQuery(id+"F0.imprint","IMPRINT",EDGE,{"derivedFrom":sQuery(id+"F0.wireOp",EDGE,"E5.4.0.2")}),1.0]])]});
            var Q76;
            Q76=makeQuery(id+"F0.imprint","IMPRINT",FACE,{"disambiguationData":[TD([[makeQuery(id+"F0.imprint","IMPRINT",EDGE,{"derivedFrom":sQuery(id+"F0.wireOp",EDGE,"E5.5.0.2")}),1.0]])]});
            var Q77;
            Q77=makeQuery(id+"F0.imprint","IMPRINT",FACE,{"disambiguationData":[TD([[makeQuery(id+"F0.imprint","IMPRINT",EDGE,{"derivedFrom":sQuery(id+"F0.wireOp",EDGE,"E5.6.0.2")}),1.0]])]});
            var Q78;
            Q78=makeQuery(id+"F0.imprint","IMPRINT",FACE,{"disambiguationData":[TD([[makeQuery(id+"F0.imprint","IMPRINT",EDGE,{"derivedFrom":sQuery(id+"F0.wireOp",EDGE,"E5.7.0.2")}),1.0]])]});
            var Q79;
            Q79=makeQuery(id+"F0.imprint","IMPRINT",FACE,{"disambiguationData":[TD([[makeQuery(id+"F0.imprint","IMPRINT",EDGE,{"derivedFrom":sQuery(id+"F0.wireOp",EDGE,"E5.8.0.2")}),1.0]])]});
            var Q80;
            Q80=makeQuery(id+"F0.imprint","IMPRINT",FACE,{"disambiguationData":[TD([[makeQuery(id+"F0.imprint","IMPRINT",EDGE,{"derivedFrom":sQuery(id+"F0.wireOp",EDGE,"E5.9.0.2")}),1.0]])]});
            var Q81;
            Q81=makeQuery(id+"F0.imprint","IMPRINT",FACE,{"disambiguationData":[TD([[makeQuery(id+"F0.imprint","IMPRINT",EDGE,{"derivedFrom":sQuery(id+"F0.wireOp",EDGE,"E5.10.0.2")}),1.0]])]});
            var Q82;
            Q82=makeQuery(id+"F0.imprint","IMPRINT",FACE,{"disambiguationData":[TD([[makeQuery(id+"F0.imprint","IMPRINT",EDGE,{"derivedFrom":sQuery(id+"F0.wireOp",EDGE,"E5.11.0.2")}),1.0]])]});
            var Q83;
            Q83=makeQuery(id+"F0.imprint","IMPRINT",FACE,{"disambiguationData":[TD([[makeQuery(id+"F0.imprint","IMPRINT",EDGE,{"derivedFrom":sQuery(id+"F0.wireOp",EDGE,"E5.12.0.2")}),1.0]])]});
            var Q84;
            Q84=makeQuery(id+"F0.imprint","IMPRINT",FACE,{"disambiguationData":[TD([[makeQuery(id+"F0.imprint","IMPRINT",EDGE,{"derivedFrom":sQuery(id+"F0.wireOp",EDGE,"E5.13.0.2")}),1.0]])]});
            var Q85;
            Q85=makeQuery(id+"F0.imprint","IMPRINT",FACE,{"disambiguationData":[TD([[makeQuery(id+"F0.imprint","IMPRINT",EDGE,{"derivedFrom":sQuery(id+"F0.wireOp",EDGE,"E5.14.0.2")}),1.0]])]});
            var Q86;
            Q86=makeQuery(id+"F0.imprint","IMPRINT",FACE,{"disambiguationData":[TD([[makeQuery(id+"F0.imprint","IMPRINT",EDGE,{"derivedFrom":sQuery(id+"F0.wireOp",EDGE,"E5.15.0.2")}),1.0]])]});
            var Q87;
            Q87=makeQuery(id+"F0.imprint","IMPRINT",FACE,{"disambiguationData":[TD([[makeQuery(id+"F0.imprint","IMPRINT",EDGE,{"derivedFrom":sQuery(id+"F0.wireOp",EDGE,"E5.16.0.2")}),1.0]])]});
            var Q88;
            Q88=makeQuery(id+"F0.imprint","IMPRINT",FACE,{"disambiguationData":[TD([[makeQuery(id+"F0.imprint","IMPRINT",EDGE,{"derivedFrom":sQuery(id+"F0.wireOp",EDGE,"E5.17.0.2")}),1.0]])]});
            var Q89;
            Q89=makeQuery(id+"F0.imprint","IMPRINT",FACE,{"disambiguationData":[TD([[makeQuery(id+"F0.imprint","IMPRINT",EDGE,{"derivedFrom":sQuery(id+"F0.wireOp",EDGE,"E5.18.0.2")}),1.0]])]});
            var Q90;
            Q90=makeQuery(id+"F0.imprint","IMPRINT",FACE,{"disambiguationData":[TD([[makeQuery(id+"F0.imprint","IMPRINT",EDGE,{"derivedFrom":sQuery(id+"F0.wireOp",EDGE,"E5.19.0.2")}),1.0]])]});
            var Q91;
            Q91=makeQuery(id+"F0.imprint","IMPRINT",FACE,{"disambiguationData":[TD([[makeQuery(id+"F0.imprint","IMPRINT",EDGE,{"derivedFrom":sQuery(id+"F0.wireOp",EDGE,"E5.19.0.3")}),1.0]])]});
            var Q92;
            Q92=makeQuery(id+"F0.imprint","IMPRINT",FACE,{"disambiguationData":[TD([[makeQuery(id+"F0.imprint","IMPRINT",EDGE,{"derivedFrom":sQuery(id+"F0.wireOp",EDGE,"E5.18.0.3")}),1.0]])]});
            var Q93;
            Q93=makeQuery(id+"F0.imprint","IMPRINT",FACE,{"disambiguationData":[TD([[makeQuery(id+"F0.imprint","IMPRINT",EDGE,{"derivedFrom":sQuery(id+"F0.wireOp",EDGE,"E5.17.0.3")}),1.0]])]});
            var Q94;
            Q94=makeQuery(id+"F0.imprint","IMPRINT",FACE,{"disambiguationData":[TD([[makeQuery(id+"F0.imprint","IMPRINT",EDGE,{"derivedFrom":sQuery(id+"F0.wireOp",EDGE,"E5.16.0.3")}),1.0]])]});
            var Q95;
            Q95=makeQuery(id+"F0.imprint","IMPRINT",FACE,{"disambiguationData":[TD([[makeQuery(id+"F0.imprint","IMPRINT",EDGE,{"derivedFrom":sQuery(id+"F0.wireOp",EDGE,"E5.15.0.3")}),1.0]])]});
            var Q96;
            Q96=makeQuery(id+"F0.imprint","IMPRINT",FACE,{"disambiguationData":[TD([[makeQuery(id+"F0.imprint","IMPRINT",EDGE,{"derivedFrom":sQuery(id+"F0.wireOp",EDGE,"E5.14.0.3")}),1.0]])]});
            var Q97;
            Q97=makeQuery(id+"F0.imprint","IMPRINT",FACE,{"disambiguationData":[TD([[makeQuery(id+"F0.imprint","IMPRINT",EDGE,{"derivedFrom":sQuery(id+"F0.wireOp",EDGE,"E5.13.0.3")}),1.0]])]});
            var Q98;
            Q98=makeQuery(id+"F0.imprint","IMPRINT",FACE,{"disambiguationData":[TD([[makeQuery(id+"F0.imprint","IMPRINT",EDGE,{"derivedFrom":sQuery(id+"F0.wireOp",EDGE,"E5.12.0.3")}),1.0]])]});
            var Q99;
            Q99=makeQuery(id+"F0.imprint","IMPRINT",FACE,{"disambiguationData":[TD([[makeQuery(id+"F0.imprint","IMPRINT",EDGE,{"derivedFrom":sQuery(id+"F0.wireOp",EDGE,"E5.11.0.3")}),1.0]])]});
            var Q100;
            Q100=makeQuery(id+"F0.imprint","IMPRINT",FACE,{"disambiguationData":[TD([[makeQuery(id+"F0.imprint","IMPRINT",EDGE,{"derivedFrom":sQuery(id+"F0.wireOp",EDGE,"E5.10.0.3")}),1.0]])]});
            var Q101;
            Q101=makeQuery(id+"F0.imprint","IMPRINT",FACE,{"disambiguationData":[TD([[makeQuery(id+"F0.imprint","IMPRINT",EDGE,{"derivedFrom":sQuery(id+"F0.wireOp",EDGE,"E5.9.0.3")}),1.0]])]});
            var Q102;
            Q102=makeQuery(id+"F0.imprint","IMPRINT",FACE,{"disambiguationData":[TD([[makeQuery(id+"F0.imprint","IMPRINT",EDGE,{"derivedFrom":sQuery(id+"F0.wireOp",EDGE,"E5.8.0.3")}),1.0]])]});
            var Q103;
            Q103=makeQuery(id+"F0.imprint","IMPRINT",FACE,{"disambiguationData":[TD([[makeQuery(id+"F0.imprint","IMPRINT",EDGE,{"derivedFrom":sQuery(id+"F0.wireOp",EDGE,"E5.7.0.3")}),1.0]])]});
            var Q104;
            Q104=makeQuery(id+"F0.imprint","IMPRINT",FACE,{"disambiguationData":[TD([[makeQuery(id+"F0.imprint","IMPRINT",EDGE,{"derivedFrom":sQuery(id+"F0.wireOp",EDGE,"E5.6.0.3")}),1.0]])]});
            var Q105;
            Q105=makeQuery(id+"F0.imprint","IMPRINT",FACE,{"disambiguationData":[TD([[makeQuery(id+"F0.imprint","IMPRINT",EDGE,{"derivedFrom":sQuery(id+"F0.wireOp",EDGE,"E5.5.0.3")}),1.0]])]});
            var Q106;
            Q106=makeQuery(id+"F0.imprint","IMPRINT",FACE,{"disambiguationData":[TD([[makeQuery(id+"F0.imprint","IMPRINT",EDGE,{"derivedFrom":sQuery(id+"F0.wireOp",EDGE,"E5.4.0.3")}),1.0]])]});
            var Q107;
            Q107=makeQuery(id+"F0.imprint","IMPRINT",FACE,{"disambiguationData":[TD([[makeQuery(id+"F0.imprint","IMPRINT",EDGE,{"derivedFrom":sQuery(id+"F0.wireOp",EDGE,"E5.3.0.3")}),1.0]])]});
            var Q108;
            Q108=makeQuery(id+"F0.imprint","IMPRINT",FACE,{"disambiguationData":[TD([[makeQuery(id+"F0.imprint","IMPRINT",EDGE,{"derivedFrom":sQuery(id+"F0.wireOp",EDGE,"E5.2.0.3")}),1.0]])]});
            var Q109;
            Q109=makeQuery(id+"F0.imprint","IMPRINT",FACE,{"disambiguationData":[TD([[makeQuery(id+"F0.imprint","IMPRINT",EDGE,{"derivedFrom":sQuery(id+"F0.wireOp",EDGE,"E5.1.0.3")}),1.0]])]});
            var Q110;
            Q110=makeQuery(id+"F0.imprint","IMPRINT",FACE,{"disambiguationData":[TD([[makeQuery(id+"F0.imprint","IMPRINT",EDGE,{"derivedFrom":sQuery(id+"F0.wireOp",EDGE,"E4.4.0.0")}),1.0]])]});
            var Q111;
            Q111=makeQuery(id+"F0.imprint","IMPRINT",FACE,{"disambiguationData":[TD([[makeQuery(id+"F0.imprint","IMPRINT",EDGE,{"derivedFrom":sQuery(id+"F0.wireOp",EDGE,"E16.1.0.0")}),1.0]])]});
            var Q112;
            Q112=makeQuery(id+"F0.imprint","IMPRINT",FACE,{"disambiguationData":[TD([[makeQuery(id+"F0.imprint","IMPRINT",EDGE,{"derivedFrom":sQuery(id+"F0.wireOp",EDGE,"E16.2.0.0")}),1.0]])]});
            var Q113;
            Q113=makeQuery(id+"F0.imprint","IMPRINT",FACE,{"disambiguationData":[TD([[makeQuery(id+"F0.imprint","IMPRINT",EDGE,{"derivedFrom":sQuery(id+"F0.wireOp",EDGE,"E16.3.0.0")}),1.0]])]});
            var Q114;
            Q114=makeQuery(id+"F0.imprint","IMPRINT",FACE,{"disambiguationData":[TD([[makeQuery(id+"F0.imprint","IMPRINT",EDGE,{"derivedFrom":sQuery(id+"F0.wireOp",EDGE,"E16.4.0.0")}),1.0]])]});
            var Q115;
            Q115=makeQuery(id+"F0.imprint","IMPRINT",FACE,{"disambiguationData":[TD([[makeQuery(id+"F0.imprint","IMPRINT",EDGE,{"derivedFrom":sQuery(id+"F0.wireOp",EDGE,"E16.5.0.0")}),1.0]])]});
            var Q116;
            Q116=makeQuery(id+"F0.imprint","IMPRINT",FACE,{"disambiguationData":[TD([[makeQuery(id+"F0.imprint","IMPRINT",EDGE,{"derivedFrom":sQuery(id+"F0.wireOp",EDGE,"E15.5.0.0")}),1.0]])]});
            var Q117;
            Q117=makeQuery(id+"F0.imprint","IMPRINT",FACE,{"disambiguationData":[TD([[makeQuery(id+"F0.imprint","IMPRINT",EDGE,{"derivedFrom":sQuery(id+"F0.wireOp",EDGE,"E15.4.0.0")}),1.0]])]});
            var Q118;
            Q118=makeQuery(id+"F0.imprint","IMPRINT",FACE,{"disambiguationData":[TD([[makeQuery(id+"F0.imprint","IMPRINT",EDGE,{"derivedFrom":sQuery(id+"F0.wireOp",EDGE,"E15.3.0.0")}),1.0]])]});
            var Q119;
            Q119=makeQuery(id+"F0.imprint","IMPRINT",FACE,{"disambiguationData":[TD([[makeQuery(id+"F0.imprint","IMPRINT",EDGE,{"derivedFrom":sQuery(id+"F0.wireOp",EDGE,"E15.2.0.0")}),1.0]])]});
            var Q120;
            Q120=makeQuery(id+"F0.imprint","IMPRINT",FACE,{"disambiguationData":[TD([[makeQuery(id+"F0.imprint","IMPRINT",EDGE,{"derivedFrom":sQuery(id+"F0.wireOp",EDGE,"E15.1.0.0")}),1.0]])]});
            var Q121;
            Q121=makeQuery(id+"F0.imprint","IMPRINT",FACE,{"disambiguationData":[TD([[makeQuery(id+"F0.imprint","IMPRINT",EDGE,{"derivedFrom":sQuery(id+"F0.wireOp",EDGE,"E4.5.0.0")}),1.0]])]});
            var Q122;
            Q122=makeQuery(id+"F0.imprint","IMPRINT",FACE,{"disambiguationData":[TD([[makeQuery(id+"F0.imprint","IMPRINT",EDGE,{"derivedFrom":sQuery(id+"F0.wireOp",EDGE,"E5.1.0.4")}),1.0]])]});
            var Q123;
            Q123=makeQuery(id+"F0.imprint","IMPRINT",FACE,{"disambiguationData":[TD([[makeQuery(id+"F0.imprint","IMPRINT",EDGE,{"derivedFrom":sQuery(id+"F0.wireOp",EDGE,"E5.2.0.4")}),1.0]])]});
            var Q124;
            Q124=makeQuery(id+"F0.imprint","IMPRINT",FACE,{"disambiguationData":[TD([[makeQuery(id+"F0.imprint","IMPRINT",EDGE,{"derivedFrom":sQuery(id+"F0.wireOp",EDGE,"E5.3.0.4")}),1.0]])]});
            var Q125;
            Q125=makeQuery(id+"F0.imprint","IMPRINT",FACE,{"disambiguationData":[TD([[makeQuery(id+"F0.imprint","IMPRINT",EDGE,{"derivedFrom":sQuery(id+"F0.wireOp",EDGE,"E5.4.0.4")}),1.0]])]});
            var Q126;
            Q126=makeQuery(id+"F0.imprint","IMPRINT",FACE,{"disambiguationData":[TD([[makeQuery(id+"F0.imprint","IMPRINT",EDGE,{"derivedFrom":sQuery(id+"F0.wireOp",EDGE,"E5.5.0.4")}),1.0]])]});
            var Q127;
            Q127=makeQuery(id+"F0.imprint","IMPRINT",FACE,{"disambiguationData":[TD([[makeQuery(id+"F0.imprint","IMPRINT",EDGE,{"derivedFrom":sQuery(id+"F0.wireOp",EDGE,"E5.6.0.4")}),1.0]])]});
            var Q128;
            Q128=makeQuery(id+"F0.imprint","IMPRINT",FACE,{"disambiguationData":[TD([[makeQuery(id+"F0.imprint","IMPRINT",EDGE,{"derivedFrom":sQuery(id+"F0.wireOp",EDGE,"E5.7.0.4")}),1.0]])]});
            var Q129;
            Q129=makeQuery(id+"F0.imprint","IMPRINT",FACE,{"disambiguationData":[TD([[makeQuery(id+"F0.imprint","IMPRINT",EDGE,{"derivedFrom":sQuery(id+"F0.wireOp",EDGE,"E5.8.0.4")}),1.0]])]});
            var Q130;
            Q130=makeQuery(id+"F0.imprint","IMPRINT",FACE,{"disambiguationData":[TD([[makeQuery(id+"F0.imprint","IMPRINT",EDGE,{"derivedFrom":sQuery(id+"F0.wireOp",EDGE,"E5.9.0.4")}),1.0]])]});
            var Q131;
            Q131=makeQuery(id+"F0.imprint","IMPRINT",FACE,{"disambiguationData":[TD([[makeQuery(id+"F0.imprint","IMPRINT",EDGE,{"derivedFrom":sQuery(id+"F0.wireOp",EDGE,"E5.10.0.4")}),1.0]])]});
            var Q132;
            Q132=makeQuery(id+"F0.imprint","IMPRINT",FACE,{"disambiguationData":[TD([[makeQuery(id+"F0.imprint","IMPRINT",EDGE,{"derivedFrom":sQuery(id+"F0.wireOp",EDGE,"E5.11.0.4")}),1.0]])]});
            var Q133;
            Q133=makeQuery(id+"F0.imprint","IMPRINT",FACE,{"disambiguationData":[TD([[makeQuery(id+"F0.imprint","IMPRINT",EDGE,{"derivedFrom":sQuery(id+"F0.wireOp",EDGE,"E5.12.0.4")}),1.0]])]});
            var Q134;
            Q134=makeQuery(id+"F0.imprint","IMPRINT",FACE,{"disambiguationData":[TD([[makeQuery(id+"F0.imprint","IMPRINT",EDGE,{"derivedFrom":sQuery(id+"F0.wireOp",EDGE,"E5.13.0.4")}),1.0]])]});
            var Q135;
            Q135=makeQuery(id+"F0.imprint","IMPRINT",FACE,{"disambiguationData":[TD([[makeQuery(id+"F0.imprint","IMPRINT",EDGE,{"derivedFrom":sQuery(id+"F0.wireOp",EDGE,"E5.14.0.4")}),1.0]])]});
            var Q136;
            Q136=makeQuery(id+"F0.imprint","IMPRINT",FACE,{"disambiguationData":[TD([[makeQuery(id+"F0.imprint","IMPRINT",EDGE,{"derivedFrom":sQuery(id+"F0.wireOp",EDGE,"E5.15.0.4")}),1.0]])]});
            var Q137;
            Q137=makeQuery(id+"F0.imprint","IMPRINT",FACE,{"disambiguationData":[TD([[makeQuery(id+"F0.imprint","IMPRINT",EDGE,{"derivedFrom":sQuery(id+"F0.wireOp",EDGE,"E5.16.0.4")}),1.0]])]});
            var Q138;
            Q138=makeQuery(id+"F0.imprint","IMPRINT",FACE,{"disambiguationData":[TD([[makeQuery(id+"F0.imprint","IMPRINT",EDGE,{"derivedFrom":sQuery(id+"F0.wireOp",EDGE,"E5.17.0.4")}),1.0]])]});
            var Q139;
            Q139=makeQuery(id+"F0.imprint","IMPRINT",FACE,{"disambiguationData":[TD([[makeQuery(id+"F0.imprint","IMPRINT",EDGE,{"derivedFrom":sQuery(id+"F0.wireOp",EDGE,"E5.18.0.4")}),1.0]])]});
            var Q140;
            Q140=makeQuery(id+"F0.imprint","IMPRINT",FACE,{"disambiguationData":[TD([[makeQuery(id+"F0.imprint","IMPRINT",EDGE,{"derivedFrom":sQuery(id+"F0.wireOp",EDGE,"E5.19.0.4")}),1.0]])]});
            extrude(context, id + "F2", {"entities" : qUnion([Q0, Q1, Q2, Q3, Q4, Q5, Q6, Q7, Q8, Q9, Q10, Q11, Q12, Q13, Q14, Q15, Q16, Q17, Q18, Q19, Q20, Q21, Q22, Q23, Q24, Q25, Q26, Q27, Q28, Q29, Q30, Q31, Q32, Q33, Q34, Q35, Q36, Q37, Q38, Q39, Q40, Q41, Q42, Q43, Q44, Q45, Q46, Q47, Q48, Q49, Q50, Q51, Q52, Q53, Q54, Q55, Q56, Q57, Q58, Q59, Q60, Q61, Q62, Q63, Q64, Q65, Q66, Q67, Q68, Q69, Q70, Q71, Q72, Q73, Q74, Q75, Q76, Q77, Q78, Q79, Q80, Q81, Q82, Q83, Q84, Q85, Q86, Q87, Q88, Q89, Q90, Q91, Q92, Q93, Q94, Q95, Q96, Q97, Q98, Q99, Q100, Q101, Q102, Q103, Q104, Q105, Q106, Q107, Q108, Q109, Q110, Q111, Q112, Q113, Q114, Q115, Q116, Q117, Q118, Q119, Q120, Q121, Q122, Q123, Q124, Q125, Q126, Q127, Q128, Q129, Q130, Q131, Q132, Q133, Q134, Q135, Q136, Q137, Q138, Q139, Q140]), "depth" : 3 * mm});
        }
    });
